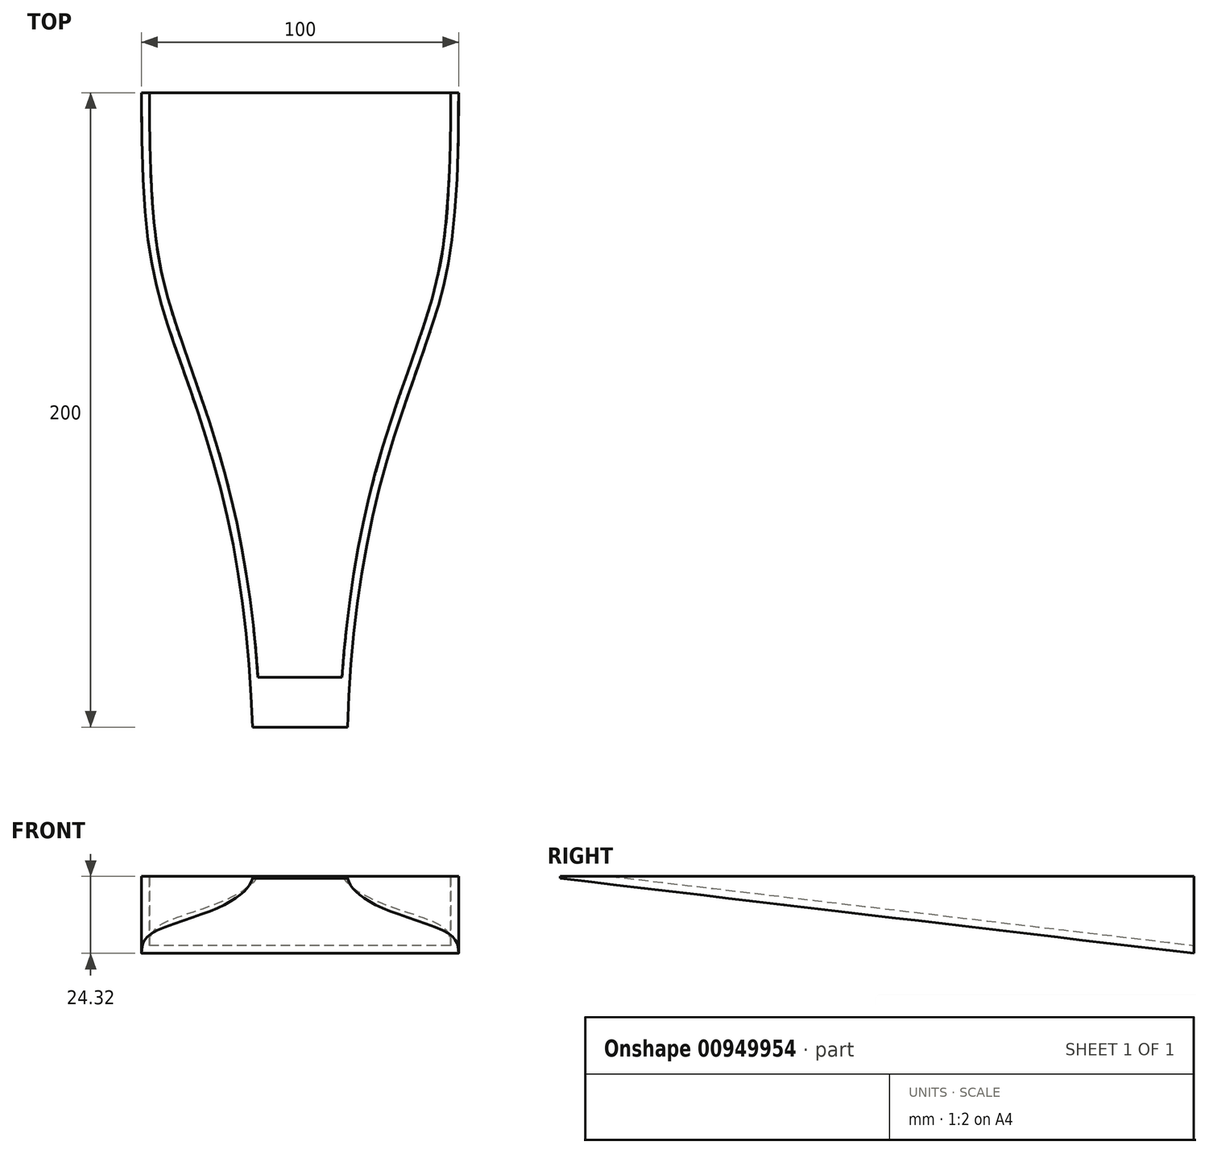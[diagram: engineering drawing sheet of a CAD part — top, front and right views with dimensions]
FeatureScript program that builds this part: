
annotation { "Feature Type Name" : "Feature", "Feature Type Description" : "" }
export const myFeature = defineFeature(function(context is Context, id is Id, definition is map)
    precondition{}
    {
        {
            var Q0;
            Q0=qCreatedBy(makeId("Top.planeOp"),FACE);
            var sketch = newSketch(context, id + "F0", { "sketchPlane" : qUnion([Q0])});
            skLineSegment(sketch, "E0", {"start": v(-50, 0) * mm, "end": v(50, 0) * mm});
            skLineSegment(sketch, "E1", {"start": v(0, 115.09) * mm, "end": v(0, -246.8) * mm, "construction": true});
            skLineSegment(sketch, "E2", {"start": v(-15, -200) * mm, "end": v(15, -200) * mm});
            skFitSpline(sketch, "E3", {"points": [v(-50, 0) * mm, v(-41.7, -73.2) * mm, v(-25.45, -123.14) * mm, v(-15, -200) * mm], "startDerivative": vector(-0.29, -369.25) * mm, "endDerivative": vector(6.65, -229.14) * mm});
            skFitSpline(sketch, "E4.MirrorCS", {"points": [v(50, 0) * mm, v(41.7, -73.2) * mm, v(25.45, -123.14) * mm, v(15, -200) * mm], "startDerivative": vector(0.29, -369.25) * mm, "endDerivative": vector(-6.65, -229.14) * mm});
            skSolve(sketch);
        }
        {
            var Q0;
            Q0=qCreatedBy(makeId("Right.planeOp"),FACE);
            var sketch = newSketch(context, id + "F1", { "sketchPlane" : qUnion([Q0])});
            skLineSegment(sketch, "E5", {"start": v(0, 0) * mm, "end": v(0, -20.02) * mm});
            skLineSegment(sketch, "E6", {"start": v(0, -20.02) * mm, "end": v(-200, 0) * mm});
            skSolve(sketch);
        }
        {
            var Q0;
            Q0=makeQuery(id+"F0.imprint","IMPRINT",FACE,{"disambiguationData":[TD([[makeQuery(id+"F0.imprint","IMPRINT",EDGE,{"derivedFrom":sQuery(id+"F0.wireOp",EDGE,"E0")}),-1.0]])]});
            extrude(context, id + "F2", {"entities" : qUnion([Q0]), "oppositeDirection" : true, "depth" : 36.9 * mm, "offsetDistance" : 25 * mm});
        }
        {
            var Q0;
            Q0=qCreatedBy(makeId("Right.planeOp"),FACE);
            var sketch = newSketch(context, id + "F3", { "sketchPlane" : qUnion([Q0])});
            skLineSegment(sketch, "E7", {"start": v(2.69, -24.64) * mm, "end": v(-215.43, 1.17) * mm});
            skLineSegment(sketch, "E8", {"start": v(-215.43, 1.17) * mm, "end": v(-215.43, -53.28) * mm});
            skLineSegment(sketch, "E9", {"start": v(-215.43, -53.28) * mm, "end": v(3.62, -53.28) * mm});
            skLineSegment(sketch, "E10", {"start": v(3.62, -53.28) * mm, "end": v(2.69, -24.64) * mm});
            skSolve(sketch);
        }
        {
            var Q0;
            Q0=makeQuery(id+"F3.imprint","IMPRINT",FACE,{"disambiguationData":[TD([[makeQuery(id+"F3.imprint","IMPRINT",EDGE,{"derivedFrom":sQuery(id+"F3.wireOp",EDGE,"E7")}),1.0]])]});
            extrude(context, id + "F4", {"entities" : qUnion([Q0]), "operationType" : NewBodyOperationType.REMOVE, "oppositeDirection" : true, "depth" : 132.4 * mm, "offsetDistance" : 25 * mm, "symmetric" : true});
        }
        {
            var Q0;
            Q0=makeQuery(id+"F2.opExtrude","CAP_FACE",FACE,{"disambiguationData":[OSD([sQuery(id+"F0.wireOp",EDGE,"E0"),sQuery(id+"F0.wireOp",EDGE,"E2"),sQuery(id+"F0.wireOp",EDGE,"E3"),sQuery(id+"F0.wireOp",EDGE,"E4.MirrorCS")])],"isStart":true});
            var Q1;
            Q1=makeQuery(id+"F2.opExtrude","SWEPT_FACE",FACE,{"disambiguationData":[OSD([sQuery(id+"F0.wireOp",EDGE,"E0")])]});
            shell(context, id + "F5", {"entities" : qUnion([Q0, Q1]), "thickness" : 2.5 * mm});
        }
    });
